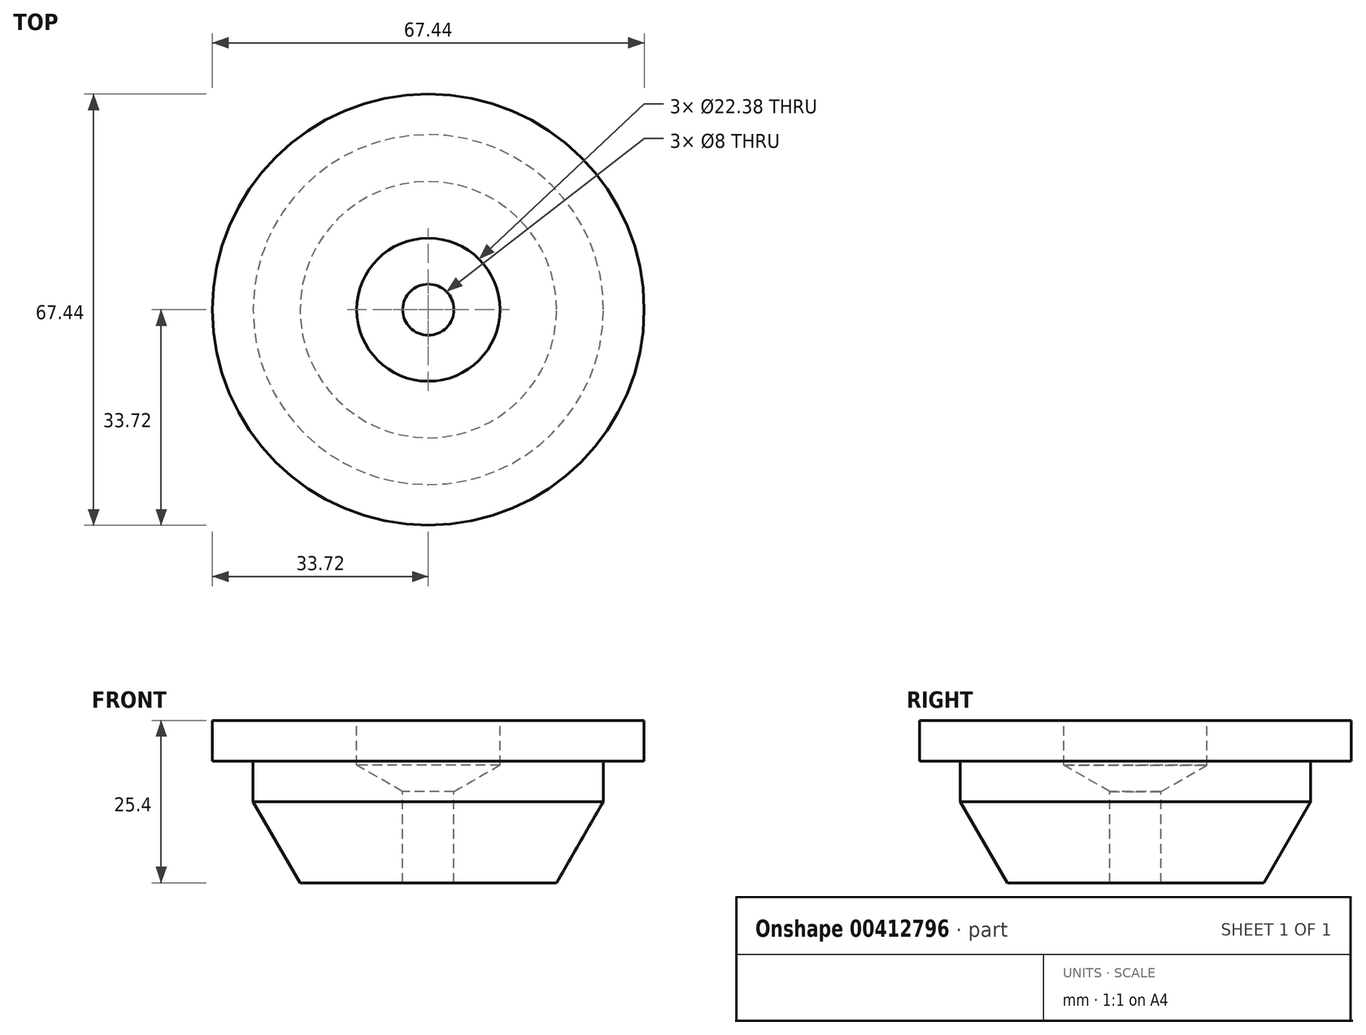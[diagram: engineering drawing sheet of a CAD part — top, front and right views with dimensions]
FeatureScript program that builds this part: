
annotation { "Feature Type Name" : "Feature", "Feature Type Description" : "" }
export const myFeature = defineFeature(function(context is Context, id is Id, definition is map)
    precondition{}
    {
        {
            var Q0;
            Q0=qCreatedBy(makeId("Front.planeOp"),FACE);
            var sketch = newSketch(context, id + "F0", { "sketchPlane" : qUnion([Q0])});
            skLineSegment(sketch, "E0", {"start": v(0, 7.32) * mm, "end": v(0, -18.08) * mm, "construction": true});
            skLineSegment(sketch, "E1", {"start": v(0, -18.08) * mm, "end": v(4, -18.08) * mm, "construction": true});
            skLineSegment(sketch, "E2", {"start": v(11.19, 7.32) * mm, "end": v(0, 7.32) * mm, "construction": true});
            skLineSegment(sketch, "E3", {"start": v(11.19, 7.32) * mm, "end": v(33.72, 7.32) * mm});
            skLineSegment(sketch, "E4", {"start": v(33.72, 7.32) * mm, "end": v(33.72, 0.97) * mm});
            skLineSegment(sketch, "E5", {"start": v(33.72, 0.97) * mm, "end": v(27.37, 0.97) * mm});
            skLineSegment(sketch, "E6", {"start": v(27.37, 0.97) * mm, "end": v(27.37, -5.38) * mm});
            skLineSegment(sketch, "E7", {"start": v(11.19, 7.32) * mm, "end": v(11.19, 0.34) * mm});
            skLineSegment(sketch, "E8", {"start": v(4, -3.81) * mm, "end": v(4, -18.08) * mm});
            skLineSegment(sketch, "E9", {"start": v(11.19, 0.34) * mm, "end": v(4, -3.81) * mm});
            skLineSegment(sketch, "E10", {"start": v(27.37, -5.38) * mm, "end": v(20.04, -18.08) * mm});
            skLineSegment(sketch, "E11", {"start": v(20.04, -18.08) * mm, "end": v(4, -18.08) * mm});
            skSolve(sketch);
        }
        {
            var Q0;
            Q0 = qSketchRegion(id + "F0", true);
            var Q1;
            Q1=sQuery(id+"F0.wireOp",EDGE,"E0");
            revolve(context, id + "F1", {"entities" : qUnion([Q0]), "axis" : qUnion([Q1]), "revolveType" : RevolveType.FULL});
        }
    });
